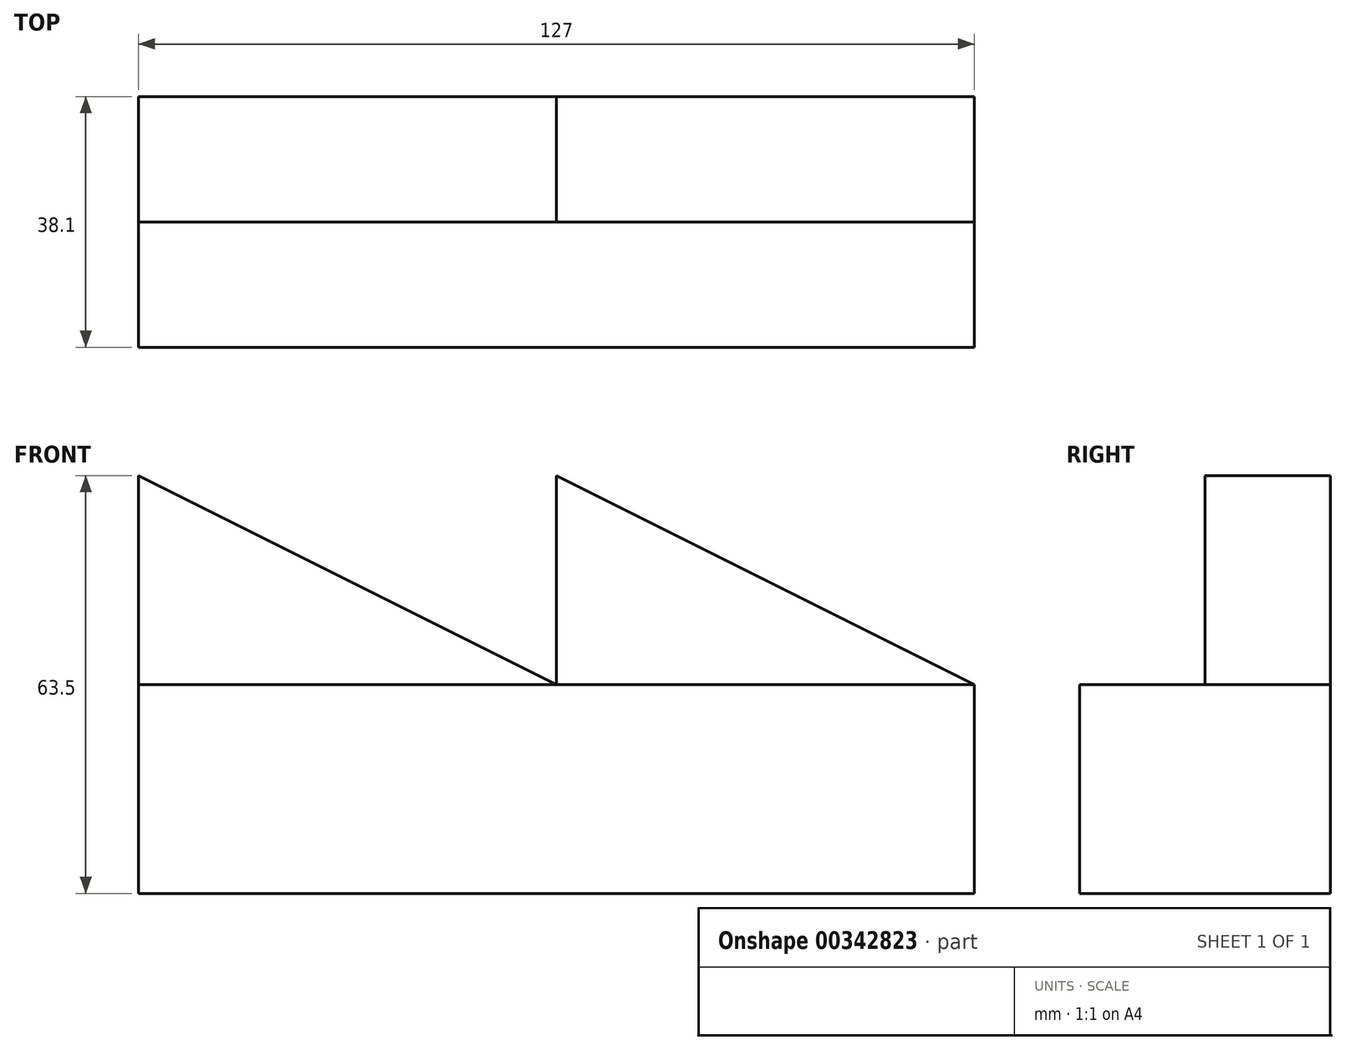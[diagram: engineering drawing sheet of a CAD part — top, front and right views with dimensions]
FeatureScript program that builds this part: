
annotation { "Feature Type Name" : "Feature", "Feature Type Description" : "" }
export const myFeature = defineFeature(function(context is Context, id is Id, definition is map)
    precondition{}
    {
        {
            var Q0;
            Q0=qCreatedBy(makeId("Front.planeOp"),FACE);
            var sketch = newSketch(context, id + "F0", { "sketchPlane" : qUnion([Q0])});
            skLineSegment(sketch, "E0", {"start": v(-55.37, -36.16) * mm, "end": v(71.63, -36.16) * mm});
            skLineSegment(sketch, "E1", {"start": v(-55.37, -36.16) * mm, "end": v(-55.37, -4.4) * mm});
            skLineSegment(sketch, "E2", {"start": v(-55.37, -4.4) * mm, "end": v(71.63, -4.4) * mm});
            skLineSegment(sketch, "E3", {"start": v(71.63, -4.4) * mm, "end": v(71.63, -36.16) * mm});
            skSolve(sketch);
        }
        {
            var Q0;
            Q0=makeQuery(id+"F0.imprint","IMPRINT",FACE,{"disambiguationData":[TD([[makeQuery(id+"F0.imprint","IMPRINT",EDGE,{"derivedFrom":sQuery(id+"F0.wireOp",EDGE,"E0")}),1.0]])]});
            extrude(context, id + "F1", {"entities" : qUnion([Q0]), "depth" : 38.1 * mm});
        }
        {
            var Q0;
            Q0=makeQuery(id+"F1.opExtrude","CAP_FACE",FACE,{"disambiguationData":[OSD([sQuery(id+"F0.wireOp",EDGE,"E0"),sQuery(id+"F0.wireOp",EDGE,"E1"),sQuery(id+"F0.wireOp",EDGE,"E2"),sQuery(id+"F0.wireOp",EDGE,"E3")])],"isStart":true});
            var sketch = newSketch(context, id + "F2", { "sketchPlane" : qUnion([Q0])});
            skLineSegment(sketch, "E4", {"start": v(55.37, -4.4) * mm, "end": v(-8.13, -4.4) * mm});
            skLineSegment(sketch, "E5", {"start": v(55.37, -4.4) * mm, "end": v(55.37, 27.34) * mm});
            skLineSegment(sketch, "E6", {"start": v(55.37, 27.34) * mm, "end": v(-8.13, -4.4) * mm});
            skLineSegment(sketch, "E7", {"start": v(-8.13, -4.4) * mm, "end": v(-8.13, 27.34) * mm});
            skLineSegment(sketch, "E8", {"start": v(-8.13, 27.34) * mm, "end": v(-71.63, -4.4) * mm});
            skLineSegment(sketch, "E9", {"start": v(-71.63, -4.4) * mm, "end": v(-8.13, -4.4) * mm});
            skSolve(sketch);
        }
        {
            var Q0;
            Q0 = qSketchRegion(id + "F2", true);
            extrude(context, id + "F3", {"entities" : qUnion([Q0]), "operationType" : NewBodyOperationType.ADD, "oppositeDirection" : true, "depth" : 19.05 * mm});
        }
    });
